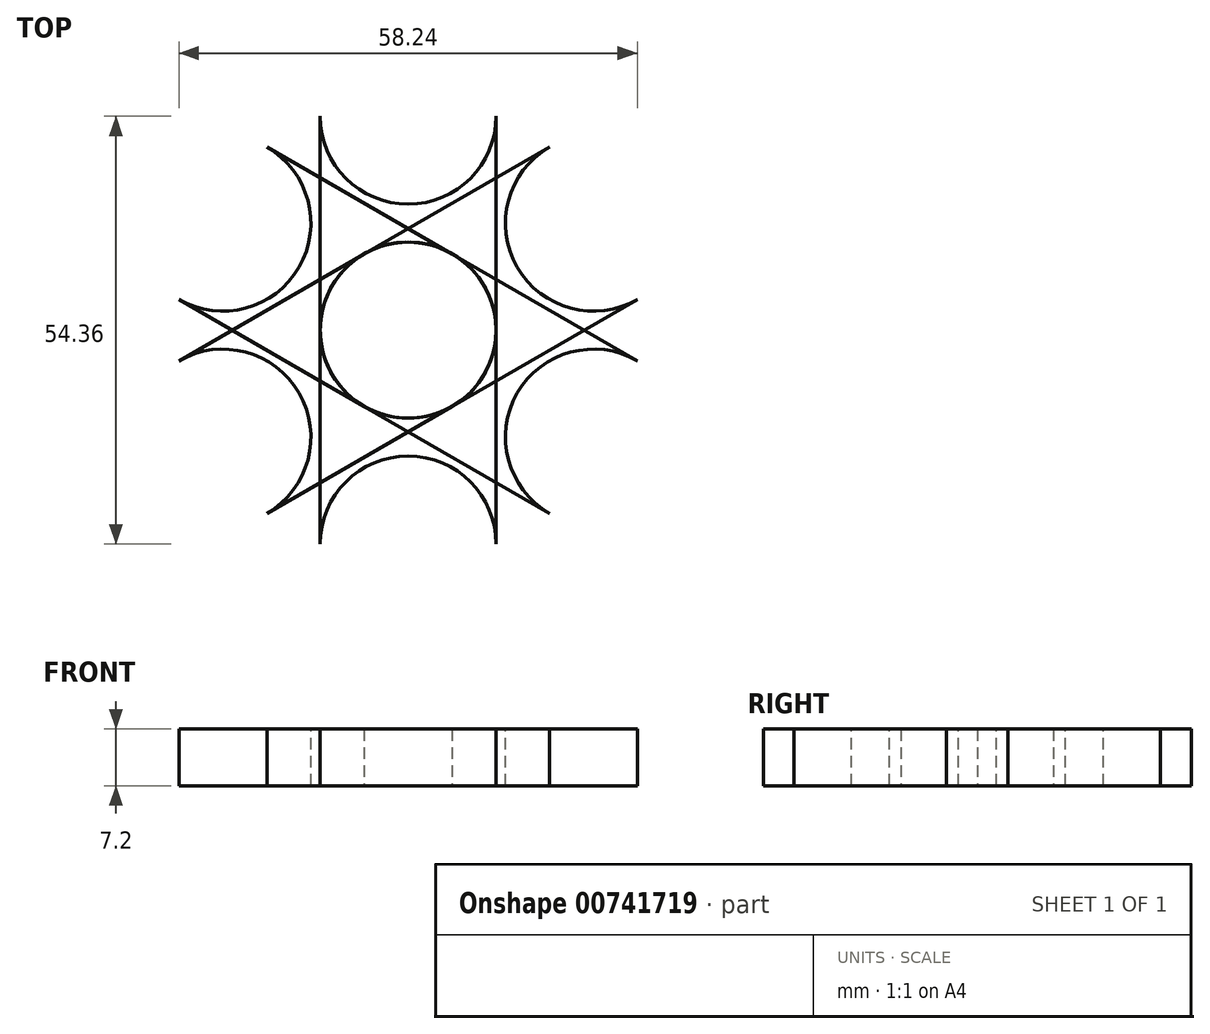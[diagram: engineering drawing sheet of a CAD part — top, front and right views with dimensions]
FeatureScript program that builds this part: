
annotation { "Feature Type Name" : "Feature", "Feature Type Description" : "" }
export const myFeature = defineFeature(function(context is Context, id is Id, definition is map)
    precondition{}
    {
        {
            var Q0;
            Q0=qCreatedBy(makeId("Top.planeOp"),FACE);
            var sketch = newSketch(context, id + "F0", { "sketchPlane" : qUnion([Q0])});
            skCircle(sketch, "E0", {"center": v(0, 0) * mm, "radius": 11.18 * mm});
            skCircle(sketch, "E1", {"center": v(0, -27.18) * mm, "radius": 11.18 * mm});
            skLineSegment(sketch, "E2", {"start": v(-11.18, 0) * mm, "end": v(-11.18, -27.18) * mm});
            skLineSegment(sketch, "E3", {"start": v(11.18, 0) * mm, "end": v(11.18, -27.18) * mm});
            skSolve(sketch);
        }
        {
            var Q0;
            Q0 = qSketchRegion(id + "F0", true);
            extrude(context, id + "F1", {"entities" : qUnion([Q0]), "depth" : 7.2 * mm, "offsetDistance" : 25.4 * mm});
        }
        {
            var Q0;
            Q0=makeQuery(id+"F1.opExtrude","CAP_FACE",FACE,{"disambiguationData":[OSD([sQuery(id+"F0.wireOp",EDGE,"E0"),sQuery(id+"F0.wireOp",EDGE,"E1"),sQuery(id+"F0.wireOp",EDGE,"E2"),sQuery(id+"F0.wireOp",EDGE,"E3")])],"isStart":false});
            var sketch = newSketch(context, id + "F2", { "sketchPlane" : qUnion([Q0])});
            skCircle(sketch, "E4", {"center": v(0, 0) * mm, "radius": 11.18 * mm});
            skLineSegment(sketch, "E5", {"start": v(-11.18, 0) * mm, "end": v(-11.18, -27.18) * mm});
            skLineSegment(sketch, "E6", {"start": v(11.18, 0) * mm, "end": v(11.18, -27.18) * mm});
            skCircle(sketch, "E7", {"center": v(0, -27.18) * mm, "radius": 11.18 * mm});
            skSolve(sketch);
        }
        {
            var Q0;
            {var subQ0=sQuery(id+"F2.wireOp",EDGE,"E4");var subQ1=makeQuery(id+"F2.imprint","INTERSECT",VERTEX,{"derivedFrom":[subQ0,sQuery(id+"F2.wireOp",EDGE,"E5")]});Q0=makeQuery(id+"F2.imprint","IMPRINT",FACE,{"disambiguationData":[TD([[makeQuery(id+"F2.imprint","IMPRINT",EDGE,{"disambiguationData":[TD([[subQ1,1.0]])],"derivedFrom":subQ0}),1.0]])]});}
            var Q1;
            {var subQ0=sQuery(id+"F2.wireOp",EDGE,"E7");var subQ1=makeQuery(id+"F2.imprint","INTERSECT",VERTEX,{"derivedFrom":[sQuery(id+"F2.wireOp",EDGE,"E5"),subQ0]});Q1=makeQuery(id+"F2.imprint","IMPRINT",FACE,{"disambiguationData":[TD([[makeQuery(id+"F2.imprint","IMPRINT",EDGE,{"disambiguationData":[TD([[subQ1,1.0]])],"derivedFrom":subQ0}),1.0]])]});}
            extrude(context, id + "F3", {"entities" : qUnion([Q0, Q1]), "operationType" : NewBodyOperationType.REMOVE, "endBound" : BoundingType.THROUGH_ALL, "oppositeDirection" : true, "depth" : 25.4 * mm, "offsetDistance" : 25.4 * mm});
        }
        {
            var Q0;
            Q0=qCreatedBy(makeId("Front.planeOp"),FACE);
            var sketch = newSketch(context, id + "F4", { "sketchPlane" : qUnion([Q0])});
            skLineSegment(sketch, "E8", {"start": v(0, 6.46) * mm, "end": v(0, 32.62) * mm});
            skSolve(sketch);
        }
        {
            var Q0;
            Q0=makeQuery(id+"F1.opExtrude","SWEPT_BODY",BODY,{"disambiguationData":[OSD([sQuery(id+"F0.wireOp",EDGE,"E0"),sQuery(id+"F0.wireOp",EDGE,"E1"),sQuery(id+"F0.wireOp",EDGE,"E2"),sQuery(id+"F0.wireOp",EDGE,"E3")])]});
            var Q1;
            Q1=sQuery(id+"F4.wireOp",EDGE,"E8");
            circularPattern(context, id + "F5", {"entities" : qUnion([Q0]), "axis" : qUnion([Q1]), "angle" : 360 * degree, "instanceCount" : 6, "equalSpace" : true});
        }
    });
